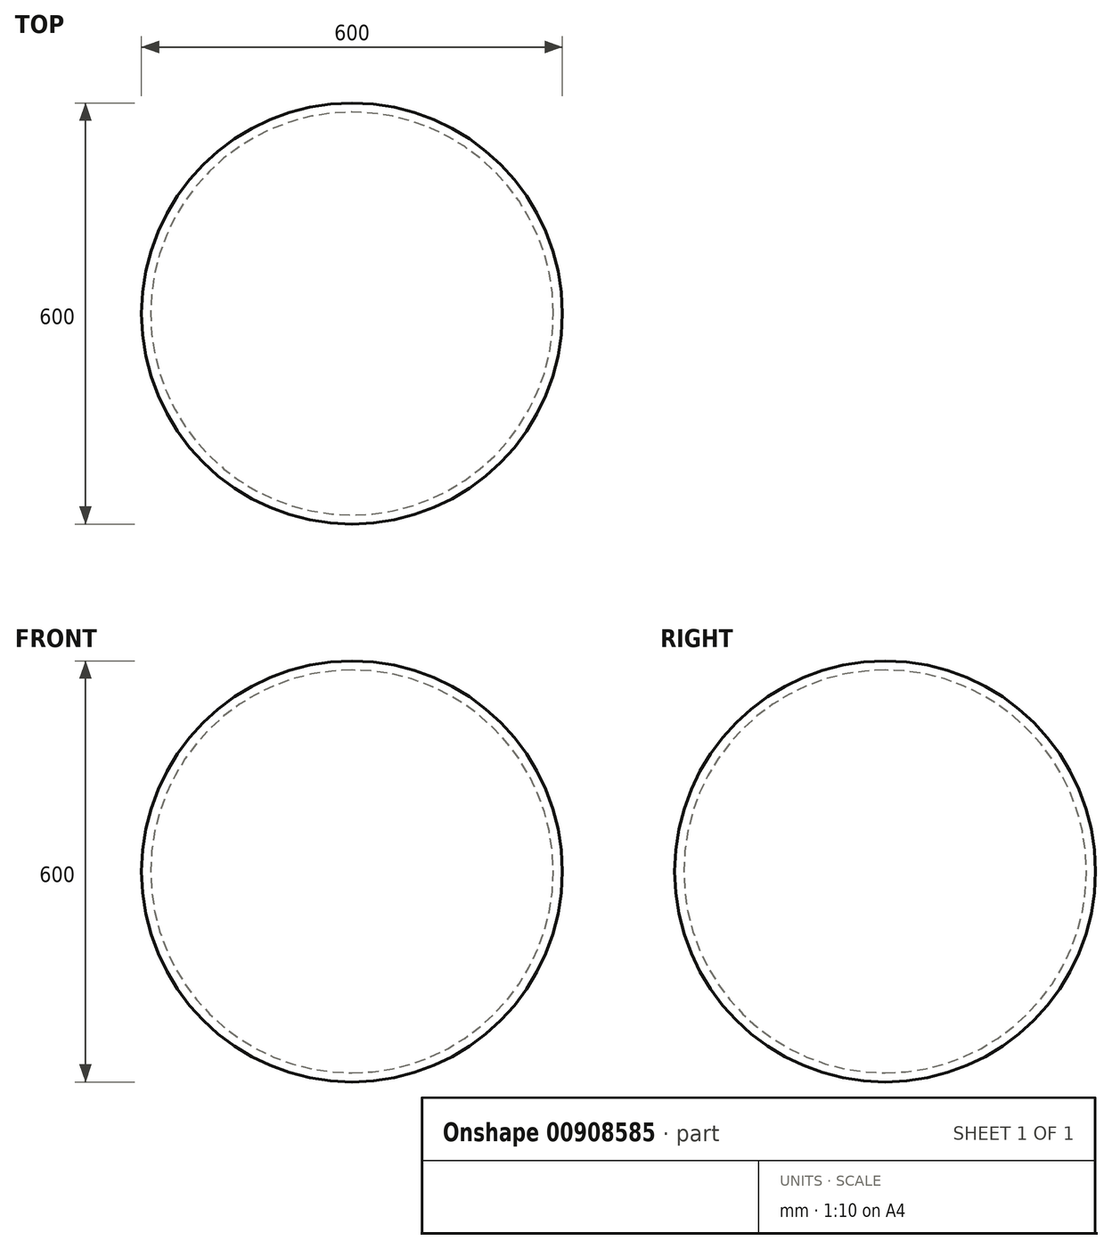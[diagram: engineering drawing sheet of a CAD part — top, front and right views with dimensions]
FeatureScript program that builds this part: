
annotation { "Feature Type Name" : "Feature", "Feature Type Description" : "" }
export const myFeature = defineFeature(function(context is Context, id is Id, definition is map)
    precondition{}
    {
        {
            var Q0;
            Q0=qCreatedBy(makeId("Front.planeOp"),FACE);
            var sketch = newSketch(context, id + "F0", { "sketchPlane" : qUnion([Q0])});
            skArc(sketch, "E0", {"start": v(0, 300) * mm, "mid": v(-300, 0) * mm, "end": v(0, -300) * mm});
            skLineSegment(sketch, "E1", {"start": v(0, 300) * mm, "end": v(0, 287) * mm});
            skLineSegment(sketch, "E2", {"start": v(0, 287) * mm, "end": v(0, -287) * mm, "construction": true});
            skLineSegment(sketch, "E3", {"start": v(0, -287) * mm, "end": v(0, -300) * mm});
            skArc(sketch, "E4", {"start": v(0, 287) * mm, "mid": v(-287, 0) * mm, "end": v(0, -287) * mm});
            skSolve(sketch);
        }
        {
            var Q0;
            Q0=makeQuery(id+"F0.imprint","IMPRINT",FACE,{"disambiguationData":[TD([[makeQuery(id+"F0.imprint","IMPRINT",EDGE,{"derivedFrom":sQuery(id+"F0.wireOp",EDGE,"E0")}),1.0]])]});
            var Q1;
            Q1=sQuery(id+"F0.wireOp",EDGE,"E2");
            revolve(context, id + "F1", {"surfaceOperationType" : NewSurfaceOperationType.NEW, "entities" : qUnion([Q0]), "axis" : qUnion([Q1]), "revolveType" : RevolveType.FULL});
        }
    });
